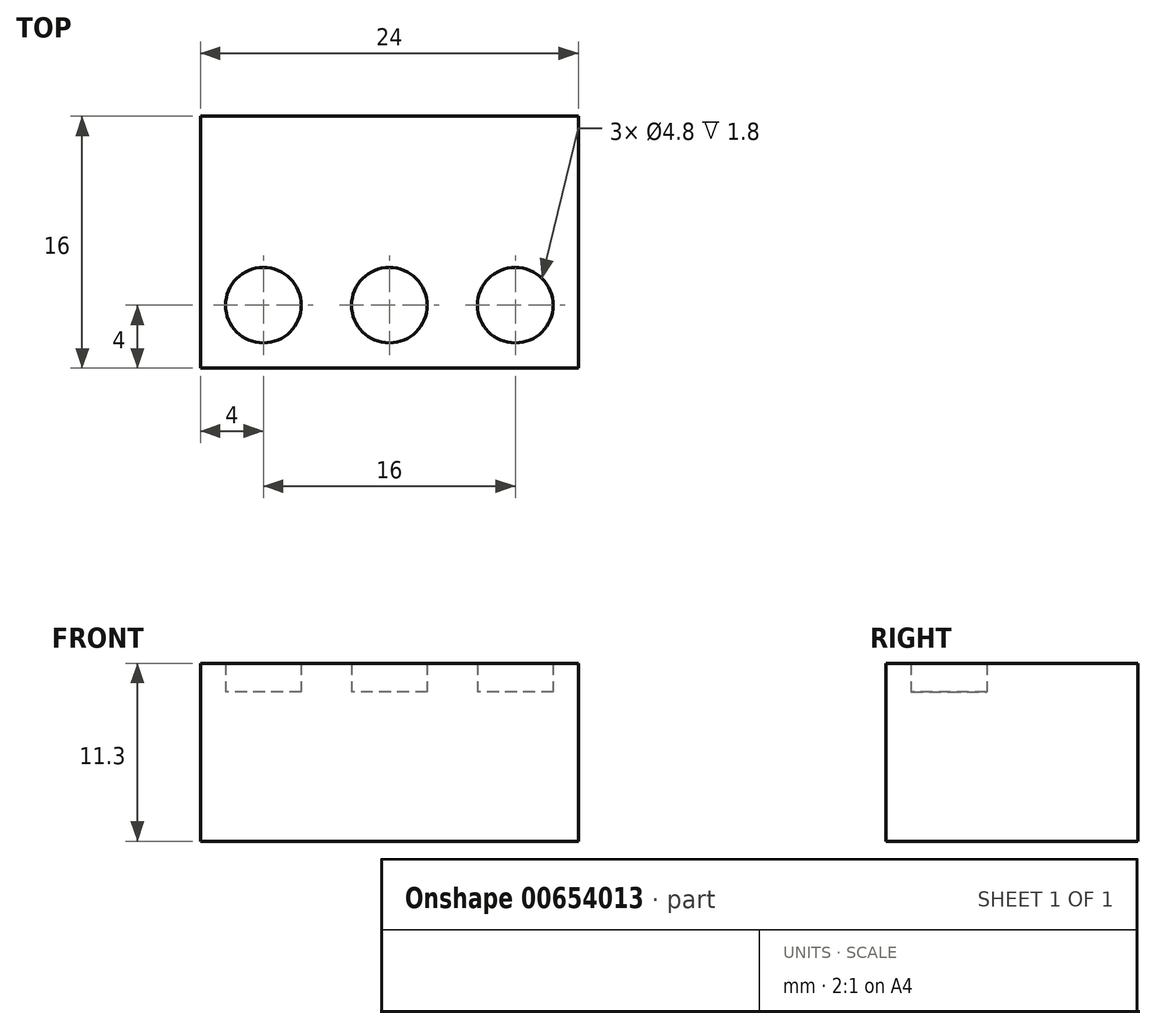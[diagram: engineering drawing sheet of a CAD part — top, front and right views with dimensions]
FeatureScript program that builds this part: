
annotation { "Feature Type Name" : "Feature", "Feature Type Description" : "" }
export const myFeature = defineFeature(function(context is Context, id is Id, definition is map)
    precondition{}
    {
        {
            var Q0;
            Q0=qCreatedBy(makeId("Top.planeOp"),FACE);
            var sketch = newSketch(context, id + "F0", { "sketchPlane" : qUnion([Q0])});
            skLineSegment(sketch, "E0.bottom", {"start": v(0, 0) * mm, "end": v(-24, 0) * mm});
            skLineSegment(sketch, "E0.top", {"start": v(0, 16) * mm, "end": v(-24, 16) * mm});
            skLineSegment(sketch, "E0.left", {"start": v(0, 0) * mm, "end": v(0, 16) * mm});
            skLineSegment(sketch, "E0.right", {"start": v(-24, 0) * mm, "end": v(-24, 16) * mm});
            skSolve(sketch);
        }
        {
            var Q0;
            Q0=makeQuery(id+"F0.imprint","IMPRINT",FACE,{"disambiguationData":[TD([[makeQuery(id+"F0.imprint","IMPRINT",EDGE,{"derivedFrom":sQuery(id+"F0.wireOp",EDGE,"E0.bottom")}),-1.0]])]});
            extrude(context, id + "F1", {"entities" : qUnion([Q0]), "depth" : 9.5 * mm, "offsetDistance" : 25.4 * mm});
        }
        {
            var Q0;
            Q0=makeQuery(id+"F1.opExtrude","CAP_FACE",FACE,{"disambiguationData":[OSD([sQuery(id+"F0.wireOp",EDGE,"E0.bottom"),sQuery(id+"F0.wireOp",EDGE,"E0.top"),sQuery(id+"F0.wireOp",EDGE,"E0.left"),sQuery(id+"F0.wireOp",EDGE,"E0.right")])],"isStart":false});
            var sketch = newSketch(context, id + "F2", { "sketchPlane" : qUnion([Q0])});
            skLineSegment(sketch, "E1", {"start": v(-24, 8) * mm, "end": v(0, 8) * mm, "construction": true});
            skLineSegment(sketch, "E2", {"start": v(-16, 16) * mm, "end": v(-16, 0) * mm});
            skLineSegment(sketch, "E3", {"start": v(-8, 16) * mm, "end": v(-8, 0) * mm, "construction": true});
            skLineSegment(sketch, "E4", {"start": v(-24, 16) * mm, "end": v(-16, 8) * mm, "construction": true});
            skLineSegment(sketch, "E5", {"start": v(-16, 8) * mm, "end": v(-8, 16) * mm, "construction": true});
            skLineSegment(sketch, "E6", {"start": v(-8, 16) * mm, "end": v(0, 8) * mm, "construction": true});
            skCircle(sketch, "E7", {"center": v(-20, 12) * mm, "radius": 2.4 * mm});
            skCircle(sketch, "E8", {"center": v(-12, 12) * mm, "radius": 2.4 * mm});
            skCircle(sketch, "E9", {"center": v(-4, 12) * mm, "radius": 2.4 * mm});
            skCircle(sketch, "E10.MirrorC", {"center": v(-20, 4) * mm, "radius": 2.4 * mm});
            skCircle(sketch, "E11.MirrorC", {"center": v(-12, 4) * mm, "radius": 2.4 * mm});
            skCircle(sketch, "E12.MirrorC", {"center": v(-4, 4) * mm, "radius": 2.4 * mm});
            skSolve(sketch);
        }
        {
            var Q0;
            Q0=makeQuery(id+"F2.imprint","IMPRINT",FACE,{"disambiguationData":[TD([[makeQuery(id+"F2.imprint","IMPRINT",EDGE,{"derivedFrom":sQuery(id+"F2.wireOp",EDGE,"E7")}),1.0]])]});
            var Q1;
            Q1=makeQuery(id+"F2.imprint","IMPRINT",FACE,{"disambiguationData":[TD([[makeQuery(id+"F2.imprint","IMPRINT",EDGE,{"derivedFrom":sQuery(id+"F2.wireOp",EDGE,"E8")}),1.0]])]});
            var Q2;
            Q2=makeQuery(id+"F2.imprint","IMPRINT",FACE,{"disambiguationData":[TD([[makeQuery(id+"F2.imprint","IMPRINT",EDGE,{"derivedFrom":sQuery(id+"F2.wireOp",EDGE,"E9")}),1.0]])]});
            var Q3;
            Q3=makeQuery(id+"F2.imprint","IMPRINT",FACE,{"disambiguationData":[TD([[makeQuery(id+"F2.imprint","IMPRINT",EDGE,{"derivedFrom":sQuery(id+"F2.wireOp",EDGE,"E10.MirrorC")}),-1.0]])]});
            var Q4;
            Q4=makeQuery(id+"F2.imprint","IMPRINT",FACE,{"disambiguationData":[TD([[makeQuery(id+"F2.imprint","IMPRINT",EDGE,{"derivedFrom":sQuery(id+"F2.wireOp",EDGE,"E11.MirrorC")}),-1.0]])]});
            var Q5;
            Q5=makeQuery(id+"F2.imprint","IMPRINT",FACE,{"disambiguationData":[TD([[makeQuery(id+"F2.imprint","IMPRINT",EDGE,{"derivedFrom":sQuery(id+"F2.wireOp",EDGE,"E12.MirrorC")}),-1.0]])]});
            extrude(context, id + "F3", {"entities" : qUnion([Q0, Q1, Q2, Q3, Q4, Q5]), "operationType" : NewBodyOperationType.ADD, "depth" : 1.8 * mm, "offsetDistance" : 25.4 * mm});
        }
    });
